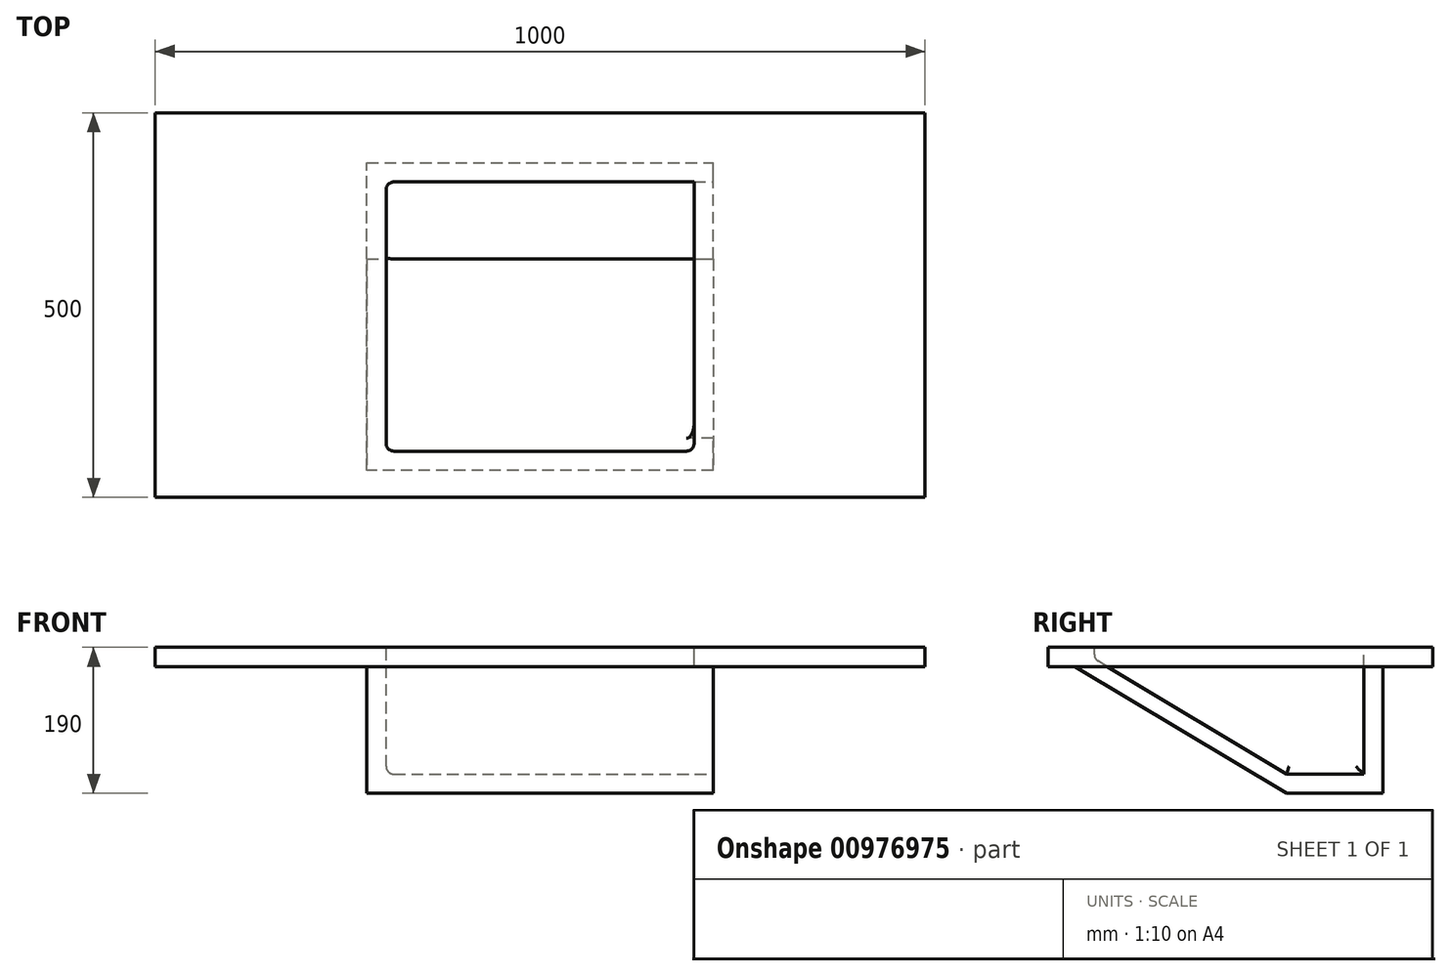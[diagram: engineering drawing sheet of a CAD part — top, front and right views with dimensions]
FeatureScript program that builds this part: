
annotation { "Feature Type Name" : "Feature", "Feature Type Description" : "" }
export const myFeature = defineFeature(function(context is Context, id is Id, definition is map)
    precondition{}
    {
        {
            var Q0;
            Q0=qCreatedBy(makeId("Top.planeOp"),FACE);
            var sketch = newSketch(context, id + "F0", { "sketchPlane" : qUnion([Q0])});
            skLineSegment(sketch, "E0.bottom", {"start": v(500, 250) * mm, "end": v(-500, 250) * mm});
            skLineSegment(sketch, "E0.top", {"start": v(500, -250) * mm, "end": v(-500, -250) * mm});
            skLineSegment(sketch, "E0.left", {"start": v(500, 250) * mm, "end": v(500, -250) * mm});
            skLineSegment(sketch, "E0.right", {"start": v(-500, 250) * mm, "end": v(-500, -250) * mm});
            skPoint(sketch, "E0.middle", {"position": v(0, 0) * mm});
            skSolve(sketch);
        }
        {
            var Q0;
            Q0 = qSketchRegion(id + "F0", true);
            extrude(context, id + "F1", {"entities" : qUnion([Q0]), "depth" : 25 * mm, "offsetDistance" : 25 * mm});
        }
        {
            var Q0;
            Q0=makeQuery(id+"F1.opExtrude","CAP_FACE",FACE,{"disambiguationData":[OSD([sQuery(id+"F0.wireOp",EDGE,"E0.bottom"),sQuery(id+"F0.wireOp",EDGE,"E0.top"),sQuery(id+"F0.wireOp",EDGE,"E0.left"),sQuery(id+"F0.wireOp",EDGE,"E0.right")])],"isStart":false});
            var sketch = newSketch(context, id + "F2", { "sketchPlane" : qUnion([Q0])});
            skLineSegment(sketch, "E1.bottom", {"start": v(-200, -190) * mm, "end": v(200, -190) * mm});
            skLineSegment(sketch, "E1.top", {"start": v(-200, 160) * mm, "end": v(200, 160) * mm});
            skLineSegment(sketch, "E1.left", {"start": v(-200, -190) * mm, "end": v(-200, 160) * mm});
            skLineSegment(sketch, "E1.right", {"start": v(200, -190) * mm, "end": v(200, 160) * mm});
            skSolve(sketch);
        }
        {
            var Q0;
            Q0 = qSketchRegion(id + "F2", true);
            extrude(context, id + "F3", {"entities" : qUnion([Q0]), "operationType" : NewBodyOperationType.REMOVE, "endBound" : BoundingType.UP_TO_NEXT, "oppositeDirection" : true, "depth" : 25 * mm, "offsetDistance" : 25 * mm});
        }
        {
            var Q0;
            Q0=makeQuery(id+"F1.opExtrude","CAP_FACE",FACE,{"disambiguationData":[OSD([sQuery(id+"F0.wireOp",EDGE,"E0.bottom"),sQuery(id+"F0.wireOp",EDGE,"E0.top"),sQuery(id+"F0.wireOp",EDGE,"E0.left"),sQuery(id+"F0.wireOp",EDGE,"E0.right")])],"isStart":true});
            var sketch = newSketch(context, id + "F4", { "sketchPlane" : qUnion([Q0])});
            skLineSegment(sketch, "E2.bottom", {"start": v(-225, -160) * mm, "end": v(225, -160) * mm});
            skLineSegment(sketch, "E2.top", {"start": v(-225, -185) * mm, "end": v(225, -185) * mm});
            skLineSegment(sketch, "E2.left", {"start": v(-225, -160) * mm, "end": v(-225, -185) * mm});
            skLineSegment(sketch, "E2.right", {"start": v(225, -160) * mm, "end": v(225, -185) * mm});
            skSolve(sketch);
        }
        {
            var Q0;
            Q0 = qSketchRegion(id + "F4", true);
            extrude(context, id + "F5", {"entities" : qUnion([Q0]), "operationType" : NewBodyOperationType.ADD, "depth" : 165 * mm, "offsetDistance" : 25 * mm});
        }
        {
            var Q0;
            Q0=makeQuery(id+"F5.boolean.opBoolean","MERGE",FACE,{"derivedFrom":[makeQuery(id+"F3.boolean.opBoolean","COPY",FACE,{"derivedFrom":makeQuery(id+"F3.opExtrude","SWEPT_FACE",FACE,{"disambiguationData":[OSD([sQuery(id+"F2.wireOp",EDGE,"E1.top")])]})}),makeQuery(id+"F5.opExtrude","SWEPT_FACE",FACE,{"disambiguationData":[OSD([sQuery(id+"F4.wireOp",EDGE,"E2.bottom")])]})]});
            var sketch = newSketch(context, id + "F6", { "sketchPlane" : qUnion([Q0])});
            skLineSegment(sketch, "E3.bottom", {"start": v(-225, -165) * mm, "end": v(225, -165) * mm});
            skLineSegment(sketch, "E3.top", {"start": v(-225, -140) * mm, "end": v(225, -140) * mm});
            skLineSegment(sketch, "E3.left", {"start": v(-225, -165) * mm, "end": v(-225, -140) * mm});
            skLineSegment(sketch, "E3.right", {"start": v(225, -165) * mm, "end": v(225, -140) * mm});
            skSolve(sketch);
        }
        {
            var Q0;
            Q0 = qSketchRegion(id + "F6", true);
            extrude(context, id + "F7", {"entities" : qUnion([Q0]), "operationType" : NewBodyOperationType.ADD, "depth" : 100 * mm, "offsetDistance" : 25 * mm});
        }
        {
            var Q0;
            Q0=makeQuery(id+"F7.boolean.opBoolean","MERGE",FACE,{"derivedFrom":[makeQuery(id+"F5.opExtrude","SWEPT_FACE",FACE,{"disambiguationData":[OSD([sQuery(id+"F4.wireOp",EDGE,"E2.left")])]}),makeQuery(id+"F7.opExtrude","SWEPT_FACE",FACE,{"disambiguationData":[OSD([sQuery(id+"F6.wireOp",EDGE,"E3.left")])]})]});
            var sketch = newSketch(context, id + "F8", { "sketchPlane" : qUnion([Q0])});
            skLineSegment(sketch, "E4", {"start": v(-185, 0) * mm, "end": v(-185, -165) * mm});
            skLineSegment(sketch, "E5", {"start": v(-185, -165) * mm, "end": v(-60, -165) * mm});
            skLineSegment(sketch, "E6", {"start": v(-60, -165) * mm, "end": v(215, 0) * mm});
            skLineSegment(sketch, "E7", {"start": v(215, 0) * mm, "end": v(-185, 0) * mm});
            skSolve(sketch);
        }
        {
            var Q0;
            Q0 = qSketchRegion(id + "F8", true);
            extrude(context, id + "F9", {"entities" : qUnion([Q0]), "operationType" : NewBodyOperationType.ADD, "oppositeDirection" : true, "depth" : 25 * mm, "offsetDistance" : 25 * mm});
        }
        {
            var Q0;
            Q0=makeQuery(id+"F9.opExtrude","SWEPT_FACE",FACE,{"disambiguationData":[OSD([sQuery(id+"F8.wireOp",EDGE,"E6")])]});
            var sketch = newSketch(context, id + "F10", { "sketchPlane" : qUnion([Q0])});
            skLineSegment(sketch, "E8.bottom", {"start": v(-225, -136.34) * mm, "end": v(225, -136.34) * mm});
            skLineSegment(sketch, "E8.top", {"start": v(-225, 184.36) * mm, "end": v(225, 184.36) * mm});
            skLineSegment(sketch, "E8.left", {"start": v(-225, -136.34) * mm, "end": v(-225, 184.36) * mm});
            skLineSegment(sketch, "E8.right", {"start": v(225, -136.34) * mm, "end": v(225, 184.36) * mm});
            skSolve(sketch);
        }
        {
            var Q0;
            Q0 = qSketchRegion(id + "F10", true);
            var Q1;
            {var subQ0=sQuery(id+"F6.wireOp",EDGE,"E3.top");Q1=makeQuery(id+"F9.boolean.opBoolean","INTERSECT",VERTEX,{"derivedFrom":[makeQuery(id+"F7.opExtrude","CAP_FACE",FACE,{"disambiguationData":[OSD([sQuery(id+"F6.wireOp",EDGE,"E3.bottom"),subQ0,sQuery(id+"F6.wireOp",EDGE,"E3.left"),sQuery(id+"F6.wireOp",EDGE,"E3.right")])],"isStart":false}),makeQuery(id+"F7.opExtrude","SWEPT_FACE",FACE,{"disambiguationData":[OSD([subQ0])]}),makeQuery(id+"F9.opExtrude","CAP_FACE",FACE,{"disambiguationData":[OSD([sQuery(id+"F8.wireOp",EDGE,"E4"),sQuery(id+"F8.wireOp",EDGE,"E5"),sQuery(id+"F8.wireOp",EDGE,"E6"),sQuery(id+"F8.wireOp",EDGE,"E7")])],"isStart":false})]});}
            extrude(context, id + "F11", {"entities" : qUnion([Q0]), "operationType" : NewBodyOperationType.ADD, "endBound" : BoundingType.UP_TO_VERTEX, "oppositeDirection" : true, "depth" : 25 * mm, "endBoundEntityVertex" : qUnion([Q1]), "offsetDistance" : 25 * mm});
        }
        {
            var Q0;
            Q0=makeQuery(id+"F7.opExtrude","CAP_EDGE",EDGE,{"disambiguationData":[OSD([sQuery(id+"F6.wireOp",EDGE,"E3.top")])],"isStart":true});
            var Q1;
            Q1=makeQuery(id+"F9.boolean.opBoolean","INTERSECT",EDGE,{"derivedFrom":[makeQuery(id+"F7.opExtrude","SWEPT_FACE",FACE,{"disambiguationData":[OSD([sQuery(id+"F6.wireOp",EDGE,"E3.top")])]}),makeQuery(id+"F9.opExtrude","CAP_FACE",FACE,{"disambiguationData":[OSD([sQuery(id+"F8.wireOp",EDGE,"E4"),sQuery(id+"F8.wireOp",EDGE,"E5"),sQuery(id+"F8.wireOp",EDGE,"E6"),sQuery(id+"F8.wireOp",EDGE,"E7")])],"isStart":false})]});
            var Q2;
            Q2=makeQuery(id+"F9.boolean.opBoolean","INTERSECT",EDGE,{"derivedFrom":[makeQuery(id+"F5.boolean.opBoolean","MERGE",FACE,{"derivedFrom":[makeQuery(id+"F3.boolean.opBoolean","COPY",FACE,{"derivedFrom":makeQuery(id+"F3.opExtrude","SWEPT_FACE",FACE,{"disambiguationData":[OSD([sQuery(id+"F2.wireOp",EDGE,"E1.top")])]})}),makeQuery(id+"F5.opExtrude","SWEPT_FACE",FACE,{"disambiguationData":[OSD([sQuery(id+"F4.wireOp",EDGE,"E2.bottom")])]})]}),makeQuery(id+"F9.opExtrude","CAP_FACE",FACE,{"disambiguationData":[OSD([sQuery(id+"F8.wireOp",EDGE,"E4"),sQuery(id+"F8.wireOp",EDGE,"E5"),sQuery(id+"F8.wireOp",EDGE,"E6"),sQuery(id+"F8.wireOp",EDGE,"E7")])],"isStart":false})]});
            var Q3;
            Q3=makeQuery(id+"FiECznerFuVCGl1_1.1.F9.boolean.opBoolean","INTERSECT",EDGE,{"derivedFrom":[makeQuery(id+"F5.boolean.opBoolean","MERGE",FACE,{"derivedFrom":[makeQuery(id+"F3.boolean.opBoolean","COPY",FACE,{"derivedFrom":makeQuery(id+"F3.opExtrude","SWEPT_FACE",FACE,{"disambiguationData":[OSD([sQuery(id+"F2.wireOp",EDGE,"E1.top")])]})}),makeQuery(id+"F5.opExtrude","SWEPT_FACE",FACE,{"disambiguationData":[OSD([sQuery(id+"F4.wireOp",EDGE,"E2.bottom")])]})]}),makeQuery(id+"FiECznerFuVCGl1_1.1.F9.opExtrude","CAP_FACE",FACE,{"disambiguationData":[OSD([sQuery(id+"F8.wireOp",EDGE,"E4"),sQuery(id+"F8.wireOp",EDGE,"E5"),sQuery(id+"F8.wireOp",EDGE,"E6"),sQuery(id+"F8.wireOp",EDGE,"E7")])],"isStart":false})]});
            var Q4;
            Q4=makeQuery(id+"FiECznerFuVCGl1_1.1.F9.boolean.opBoolean","INTERSECT",EDGE,{"derivedFrom":[makeQuery(id+"F7.opExtrude","SWEPT_FACE",FACE,{"disambiguationData":[OSD([sQuery(id+"F6.wireOp",EDGE,"E3.top")])]}),makeQuery(id+"FiECznerFuVCGl1_1.1.F9.opExtrude","CAP_FACE",FACE,{"disambiguationData":[OSD([sQuery(id+"F8.wireOp",EDGE,"E4"),sQuery(id+"F8.wireOp",EDGE,"E5"),sQuery(id+"F8.wireOp",EDGE,"E6"),sQuery(id+"F8.wireOp",EDGE,"E7")])],"isStart":false})]});
            var Q5;
            Q5=makeQuery(id+"F11.boolean.opBoolean","INTERSECT",EDGE,{"derivedFrom":[makeQuery(id+"FiECznerFuVCGl1_1.1.F9.boolean.opBoolean","MERGE",FACE,{"derivedFrom":[makeQuery(id+"F3.boolean.opBoolean","COPY",FACE,{"derivedFrom":makeQuery(id+"F3.opExtrude","SWEPT_FACE",FACE,{"disambiguationData":[OSD([sQuery(id+"F2.wireOp",EDGE,"E1.right")])]})}),makeQuery(id+"FiECznerFuVCGl1_1.1.F9.opExtrude","CAP_FACE",FACE,{"disambiguationData":[OSD([sQuery(id+"F8.wireOp",EDGE,"E4"),sQuery(id+"F8.wireOp",EDGE,"E5"),sQuery(id+"F8.wireOp",EDGE,"E6"),sQuery(id+"F8.wireOp",EDGE,"E7")])],"isStart":false})]}),makeQuery(id+"F11.opExtrude","CAP_FACE",FACE,{"disambiguationData":[OSD([sQuery(id+"F10.wireOp",EDGE,"E8.bottom"),sQuery(id+"F10.wireOp",EDGE,"E8.top"),sQuery(id+"F10.wireOp",EDGE,"E8.left"),sQuery(id+"F10.wireOp",EDGE,"E8.right")])],"isStart":false})]});
            var Q6;
            Q6=makeQuery(id+"F7.opExtrude","CAP_EDGE",EDGE,{"disambiguationData":[OSD([sQuery(id+"F6.wireOp",EDGE,"E3.top")])],"isStart":false});
            var Q7;
            Q7=makeQuery(id+"F11.boolean.opBoolean","INTERSECT",EDGE,{"derivedFrom":[makeQuery(id+"F9.boolean.opBoolean","MERGE",FACE,{"derivedFrom":[makeQuery(id+"F3.boolean.opBoolean","COPY",FACE,{"derivedFrom":makeQuery(id+"F3.opExtrude","SWEPT_FACE",FACE,{"disambiguationData":[OSD([sQuery(id+"F2.wireOp",EDGE,"E1.left")])]})}),makeQuery(id+"F9.opExtrude","CAP_FACE",FACE,{"disambiguationData":[OSD([sQuery(id+"F8.wireOp",EDGE,"E4"),sQuery(id+"F8.wireOp",EDGE,"E5"),sQuery(id+"F8.wireOp",EDGE,"E6"),sQuery(id+"F8.wireOp",EDGE,"E7")])],"isStart":false})]}),makeQuery(id+"F11.opExtrude","CAP_FACE",FACE,{"disambiguationData":[OSD([sQuery(id+"F10.wireOp",EDGE,"E8.bottom"),sQuery(id+"F10.wireOp",EDGE,"E8.top"),sQuery(id+"F10.wireOp",EDGE,"E8.left"),sQuery(id+"F10.wireOp",EDGE,"E8.right")])],"isStart":false})]});
            var Q8;
            Q8=makeQuery(id+"F3.boolean.opBoolean","COPY",EDGE,{"derivedFrom":makeQuery(id+"F3.opExtrude","SWEPT_EDGE",EDGE,{"disambiguationData":[OSD([sQuery(id+"F2.wireOp",EDGE,"E1.bottom"),sQuery(id+"F2.wireOp",EDGE,"E1.left")])]})});
            var Q9;
            Q9=makeQuery(id+"F3.boolean.opBoolean","COPY",EDGE,{"derivedFrom":makeQuery(id+"F3.opExtrude","SWEPT_EDGE",EDGE,{"disambiguationData":[OSD([sQuery(id+"F2.wireOp",EDGE,"E1.bottom"),sQuery(id+"F2.wireOp",EDGE,"E1.right")])]})});
            var Q10;
            Q10=makeQuery(id+"F11.boolean.opBoolean","INTERSECT",EDGE,{"derivedFrom":[makeQuery(id+"F3.boolean.opBoolean","COPY",FACE,{"derivedFrom":makeQuery(id+"F3.opExtrude","SWEPT_FACE",FACE,{"disambiguationData":[OSD([sQuery(id+"F2.wireOp",EDGE,"E1.bottom")])]})}),makeQuery(id+"F11.opExtrude","CAP_FACE",FACE,{"disambiguationData":[OSD([sQuery(id+"F10.wireOp",EDGE,"E8.bottom"),sQuery(id+"F10.wireOp",EDGE,"E8.top"),sQuery(id+"F10.wireOp",EDGE,"E8.left"),sQuery(id+"F10.wireOp",EDGE,"E8.right")])],"isStart":false})]});
            fillet(context, id + "F12", {"entities" : qUnion([Q0, Q1, Q2, Q3, Q4, Q5, Q6, Q7, Q8, Q9, Q10]), "radius" : 10 * mm, "tangentPropagation" : true, "allowEdgeOverflow" : false});
        }
    });
